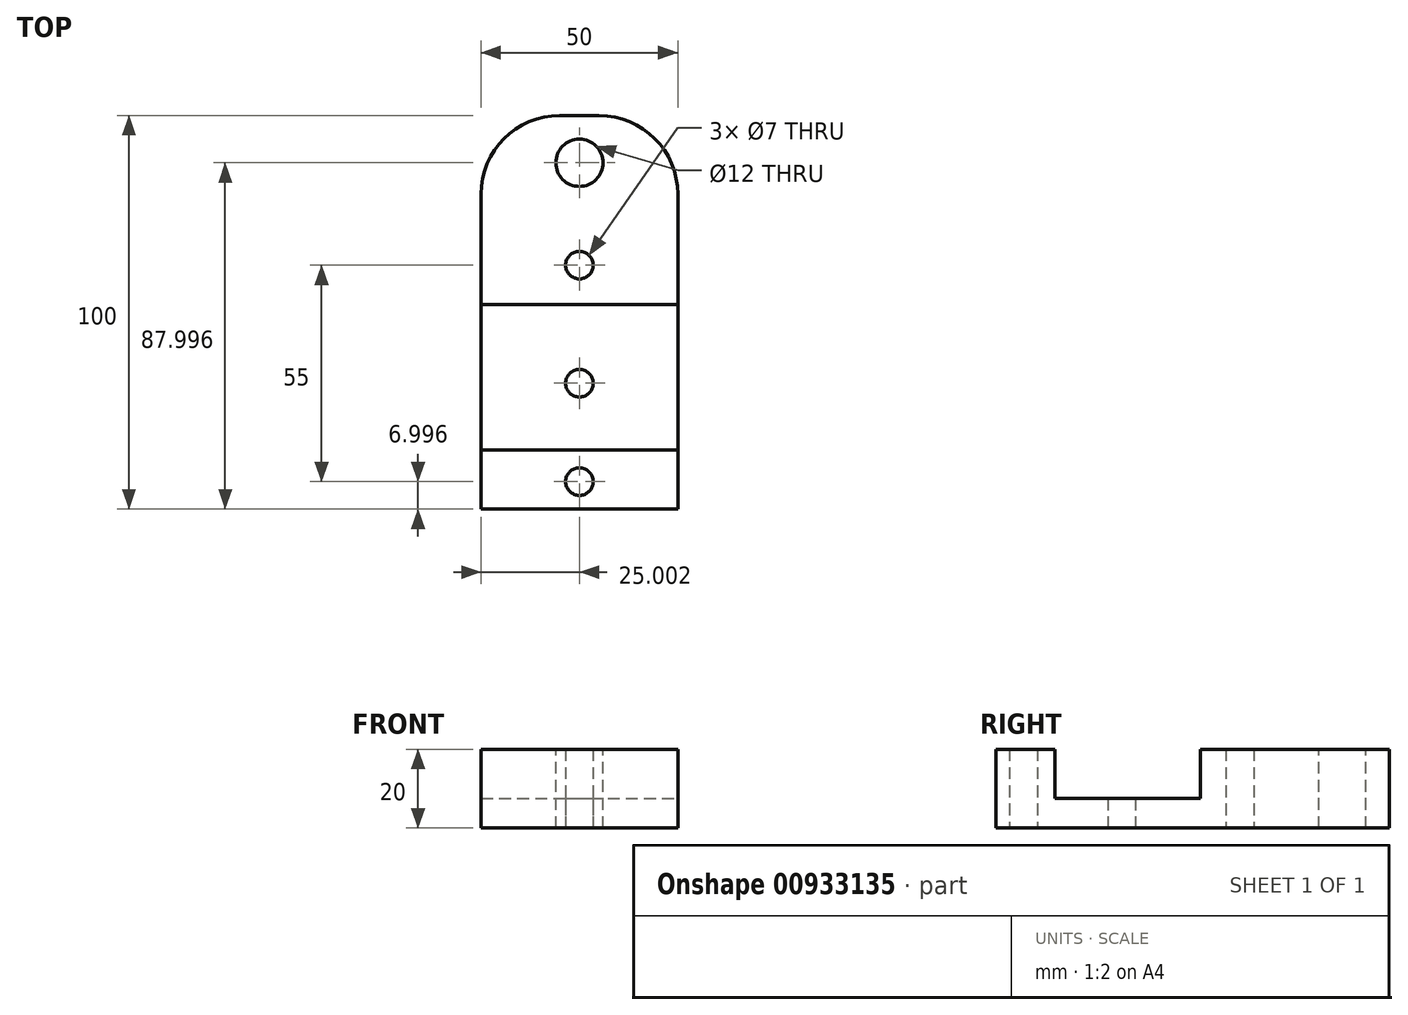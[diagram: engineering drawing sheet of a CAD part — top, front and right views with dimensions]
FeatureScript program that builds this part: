
annotation { "Feature Type Name" : "Feature", "Feature Type Description" : "" }
export const myFeature = defineFeature(function(context is Context, id is Id, definition is map)
    precondition{}
    {
        {
            var Q0;
            Q0=qCreatedBy(makeId("Top.planeOp"),FACE);
            var sketch = newSketch(context, id + "F0", { "sketchPlane" : qUnion([Q0])});
            skLineSegment(sketch, "E0.bottom", {"start": v(-18.79, 16.64) * mm, "end": v(31.21, 16.64) * mm});
            skLineSegment(sketch, "E0.top", {"start": v(-18.79, -83.36) * mm, "end": v(31.21, -83.36) * mm});
            skLineSegment(sketch, "E0.left", {"start": v(-18.79, 16.64) * mm, "end": v(-18.79, -83.36) * mm});
            skLineSegment(sketch, "E0.right", {"start": v(31.21, 16.64) * mm, "end": v(31.21, -83.36) * mm});
            skSolve(sketch);
        }
        {
            var Q0;
            Q0 = qSketchRegion(id + "F0", true);
            extrude(context, id + "F1", {"entities" : qUnion([Q0]), "depth" : 20 * mm, "offsetDistance" : 25 * mm});
        }
        {
            var Q0;
            Q0=makeQuery(id+"F1.opExtrude","CAP_FACE",FACE,{"disambiguationData":[OSD([sQuery(id+"F0.wireOp",EDGE,"E0.bottom"),sQuery(id+"F0.wireOp",EDGE,"E0.top"),sQuery(id+"F0.wireOp",EDGE,"E0.left"),sQuery(id+"F0.wireOp",EDGE,"E0.right")])],"isStart":false});
            var sketch = newSketch(context, id + "F2", { "sketchPlane" : qUnion([Q0])});
            skCircle(sketch, "E1", {"center": v(6.21, 4.64) * mm, "radius": 6 * mm});
            skSolve(sketch);
        }
        {
            var Q0;
            Q0 = qSketchRegion(id + "F2", true);
            extrude(context, id + "F3", {"entities" : qUnion([Q0]), "operationType" : NewBodyOperationType.REMOVE, "oppositeDirection" : true, "depth" : 25 * mm, "offsetDistance" : 25 * mm});
        }
        {
            var Q0;
            Q0=makeQuery(id+"F1.opExtrude","SWEPT_EDGE",EDGE,{"disambiguationData":[OSD([sQuery(id+"F0.wireOp",EDGE,"E0.bottom"),sQuery(id+"F0.wireOp",EDGE,"E0.right")])]});
            fillet(context, id + "F4", {"entities" : qUnion([Q0]), "radius" : 20 * mm, "tangentPropagation" : true, "allowEdgeOverflow" : false});
        }
        {
            var Q0;
            Q0=makeQuery(id+"F1.opExtrude","SWEPT_EDGE",EDGE,{"disambiguationData":[OSD([sQuery(id+"F0.wireOp",EDGE,"E0.bottom"),sQuery(id+"F0.wireOp",EDGE,"E0.left")])]});
            fillet(context, id + "F5", {"entities" : qUnion([Q0]), "radius" : 20 * mm, "tangentPropagation" : true, "allowEdgeOverflow" : false});
        }
        {
            var Q0;
            Q0=makeQuery(id+"F1.opExtrude","SWEPT_FACE",FACE,{"disambiguationData":[OSD([sQuery(id+"F0.wireOp",EDGE,"E0.right")])]});
            var sketch = newSketch(context, id + "F6", { "sketchPlane" : qUnion([Q0])});
            skLineSegment(sketch, "E2.bottom", {"start": v(-68.36, 20) * mm, "end": v(-31.36, 20) * mm});
            skLineSegment(sketch, "E2.top", {"start": v(-68.36, 7.5) * mm, "end": v(-31.36, 7.5) * mm});
            skLineSegment(sketch, "E2.left", {"start": v(-68.36, 20) * mm, "end": v(-68.36, 7.5) * mm});
            skLineSegment(sketch, "E2.right", {"start": v(-31.36, 20) * mm, "end": v(-31.36, 7.5) * mm});
            skSolve(sketch);
        }
        {
            var Q0;
            Q0 = qSketchRegion(id + "F6", true);
            extrude(context, id + "F7", {"entities" : qUnion([Q0]), "operationType" : NewBodyOperationType.REMOVE, "endBound" : BoundingType.THROUGH_ALL, "oppositeDirection" : true, "depth" : 25 * mm, "offsetDistance" : 25 * mm});
        }
        {
            var Q0;
            Q0=makeQuery(id+"F1.opExtrude","CAP_FACE",FACE,{"disambiguationData":[OSD([sQuery(id+"F0.wireOp",EDGE,"E0.bottom"),sQuery(id+"F0.wireOp",EDGE,"E0.top"),sQuery(id+"F0.wireOp",EDGE,"E0.left"),sQuery(id+"F0.wireOp",EDGE,"E0.right")])],"isStart":true});
            var sketch = newSketch(context, id + "F8", { "sketchPlane" : qUnion([Q0])});
            skLineSegment(sketch, "E3", {"start": v(6.21, -4.64) * mm, "end": v(6.21, 76.36) * mm, "construction": true});
            skCircle(sketch, "E4", {"center": v(6.21, 76.36) * mm, "radius": 3.5 * mm});
            skCircle(sketch, "E5", {"center": v(6.21, 21.36) * mm, "radius": 3.5 * mm});
            skCircle(sketch, "E6", {"center": v(6.21, 51.36) * mm, "radius": 3.5 * mm});
            skSolve(sketch);
        }
        {
            var Q0;
            Q0=makeQuery(id+"F8.imprint","IMPRINT",FACE,{"disambiguationData":[TD([[makeQuery(id+"F8.imprint","IMPRINT",EDGE,{"derivedFrom":sQuery(id+"F8.wireOp",EDGE,"E6")}),1.0]])]});
            var Q1;
            Q1=makeQuery(id+"F8.imprint","IMPRINT",FACE,{"disambiguationData":[TD([[makeQuery(id+"F8.imprint","IMPRINT",EDGE,{"derivedFrom":sQuery(id+"F8.wireOp",EDGE,"E5")}),1.0]])]});
            var Q2;
            Q2=makeQuery(id+"F8.imprint","IMPRINT",FACE,{"disambiguationData":[TD([[makeQuery(id+"F8.imprint","IMPRINT",EDGE,{"derivedFrom":sQuery(id+"F8.wireOp",EDGE,"E4")}),1.0]])]});
            extrude(context, id + "F9", {"entities" : qUnion([Q0, Q1, Q2]), "operationType" : NewBodyOperationType.REMOVE, "endBound" : BoundingType.THROUGH_ALL, "oppositeDirection" : true, "depth" : 25 * mm, "offsetDistance" : 25 * mm});
        }
    });
